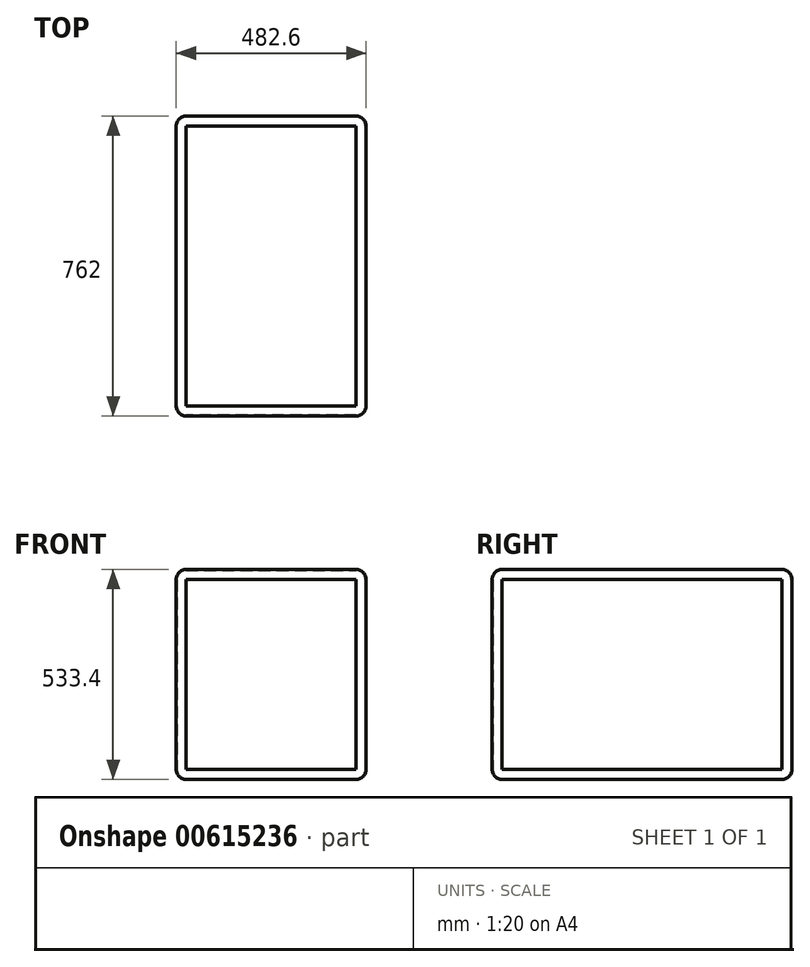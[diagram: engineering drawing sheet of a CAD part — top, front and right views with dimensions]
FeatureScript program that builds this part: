
annotation { "Feature Type Name" : "Feature", "Feature Type Description" : "" }
export const myFeature = defineFeature(function(context is Context, id is Id, definition is map)
    precondition{}
    {
        {
            var Q0;
            Q0=qCreatedBy(makeId("Front.planeOp"),FACE);
            var sketch = newSketch(context, id + "F0", { "sketchPlane" : qUnion([Q0])});
            skLineSegment(sketch, "E0.bottom", {"start": v(0, 0) * mm, "end": v(482.6, 0) * mm});
            skLineSegment(sketch, "E0.top", {"start": v(0, 533.4) * mm, "end": v(482.6, 533.4) * mm});
            skLineSegment(sketch, "E0.left", {"start": v(0, 0) * mm, "end": v(0, 533.4) * mm});
            skLineSegment(sketch, "E0.right", {"start": v(482.6, 0) * mm, "end": v(482.6, 533.4) * mm});
            skSolve(sketch);
        }
        {
            var Q0;
            Q0=makeQuery(id+"F0.imprint","IMPRINT",FACE,{"disambiguationData":[TD([[makeQuery(id+"F0.imprint","IMPRINT",EDGE,{"derivedFrom":sQuery(id+"F0.wireOp",EDGE,"E0.bottom")}),1.0]])]});
            extrude(context, id + "F1", {"entities" : qUnion([Q0]), "depth" : 762 * mm, "offsetDistance" : 25.4 * mm});
        }
        {
            var Q0;
            Q0=makeQuery(id+"F1.opExtrude","SWEPT_EDGE",EDGE,{"disambiguationData":[OSD([sQuery(id+"F0.wireOp",EDGE,"E0.top"),sQuery(id+"F0.wireOp",EDGE,"E0.right")])]});
            var Q1;
            Q1=makeQuery(id+"F1.opExtrude","CAP_EDGE",EDGE,{"disambiguationData":[OSD([sQuery(id+"F0.wireOp",EDGE,"E0.right")])],"isStart":false});
            var Q2;
            Q2=makeQuery(id+"F1.opExtrude","SWEPT_FACE",FACE,{"disambiguationData":[OSD([sQuery(id+"F0.wireOp",EDGE,"E0.top")])]});
            var Q3;
            Q3=makeQuery(id+"F1.opExtrude","CAP_EDGE",EDGE,{"disambiguationData":[OSD([sQuery(id+"F0.wireOp",EDGE,"E0.top")])],"isStart":false});
            var Q4;
            Q4=makeQuery(id+"F1.opExtrude","CAP_EDGE",EDGE,{"disambiguationData":[OSD([sQuery(id+"F0.wireOp",EDGE,"E0.bottom")])],"isStart":false});
            var Q5;
            Q5=makeQuery(id+"F1.opExtrude","SWEPT_EDGE",EDGE,{"disambiguationData":[OSD([sQuery(id+"F0.wireOp",EDGE,"E0.bottom"),sQuery(id+"F0.wireOp",EDGE,"E0.right")])]});
            var Q6;
            Q6=makeQuery(id+"F1.opExtrude","CAP_EDGE",EDGE,{"disambiguationData":[OSD([sQuery(id+"F0.wireOp",EDGE,"E0.right")])],"isStart":true});
            var Q7;
            Q7=makeQuery(id+"F1.opExtrude","CAP_EDGE",EDGE,{"disambiguationData":[OSD([sQuery(id+"F0.wireOp",EDGE,"E0.top")])],"isStart":true});
            var Q8;
            Q8=makeQuery(id+"F1.opExtrude","CAP_EDGE",EDGE,{"disambiguationData":[OSD([sQuery(id+"F0.wireOp",EDGE,"E0.left")])],"isStart":true});
            var Q9;
            Q9=makeQuery(id+"F1.opExtrude","CAP_EDGE",EDGE,{"disambiguationData":[OSD([sQuery(id+"F0.wireOp",EDGE,"E0.bottom")])],"isStart":true});
            var Q10;
            Q10=makeQuery(id+"F1.opExtrude","SWEPT_EDGE",EDGE,{"disambiguationData":[OSD([sQuery(id+"F0.wireOp",EDGE,"E0.bottom"),sQuery(id+"F0.wireOp",EDGE,"E0.left")])]});
            var Q11;
            Q11=makeQuery(id+"F1.opExtrude","CAP_EDGE",EDGE,{"disambiguationData":[OSD([sQuery(id+"F0.wireOp",EDGE,"E0.left")])],"isStart":false});
            fillet(context, id + "F2", {"entities" : qUnion([Q0, Q1, Q2, Q3, Q4, Q5, Q6, Q7, Q8, Q9, Q10, Q11]), "radius" : 25.4 * mm, "tangentPropagation" : true, "allowEdgeOverflow" : false});
        }
        {
            var Q0;
            Q0=makeQuery(id+"F1.opExtrude","CAP_FACE",FACE,{"disambiguationData":[OSD([sQuery(id+"F0.wireOp",EDGE,"E0.bottom"),sQuery(id+"F0.wireOp",EDGE,"E0.top"),sQuery(id+"F0.wireOp",EDGE,"E0.left"),sQuery(id+"F0.wireOp",EDGE,"E0.right")])],"isStart":true});
            var Q1;
            Q1=makeQuery(id+"F1.opExtrude","CAP_FACE",FACE,{"disambiguationData":[OSD([sQuery(id+"F0.wireOp",EDGE,"E0.bottom"),sQuery(id+"F0.wireOp",EDGE,"E0.top"),sQuery(id+"F0.wireOp",EDGE,"E0.left"),sQuery(id+"F0.wireOp",EDGE,"E0.right")])],"isStart":false});
            var Q2;
            Q2=makeQuery(id+"F1.opExtrude","SWEPT_FACE",FACE,{"disambiguationData":[OSD([sQuery(id+"F0.wireOp",EDGE,"E0.right")])]});
            var Q3;
            Q3=makeQuery(id+"F1.opExtrude","SWEPT_FACE",FACE,{"disambiguationData":[OSD([sQuery(id+"F0.wireOp",EDGE,"E0.top")])]});
            var Q4;
            Q4=makeQuery(id+"F1.opExtrude","SWEPT_FACE",FACE,{"disambiguationData":[OSD([sQuery(id+"F0.wireOp",EDGE,"E0.left")])]});
            shell(context, id + "F3", {"entities" : qUnion([Q0, Q1, Q2, Q3, Q4]), "thickness" : 2.54 * mm});
        }
    });
